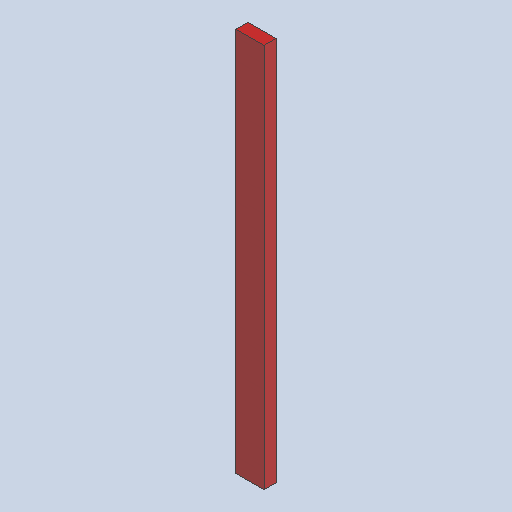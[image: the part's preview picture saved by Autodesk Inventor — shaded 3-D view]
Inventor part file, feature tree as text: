
AUTODESK INVENTOR PART (.ipt)
format: ipt  version: 2025.1 (Build 291241020, 241B)  size: 253,440 bytes
history: native  units: in
note: dims shown in document units (in); Inventor stores cm internally (conversion verified against a paired STEP export)
features: extrude x1, sketch x1, other x1
ambient origin geometry x8: Origin, YZ Plane, XZ Plane, XY Plane, X Axis, Y Axis, Z Axis, Center Point
bodies: Solid1 (feature_tree)
feature tree (3):
  extrude  "Extrusion1"  Depth=3.5in
  sketch  "Sketch1"  dims[d0=1.5in d1=3.5in d2=48.0in d3=0.0in]
  other  "Finish1"
